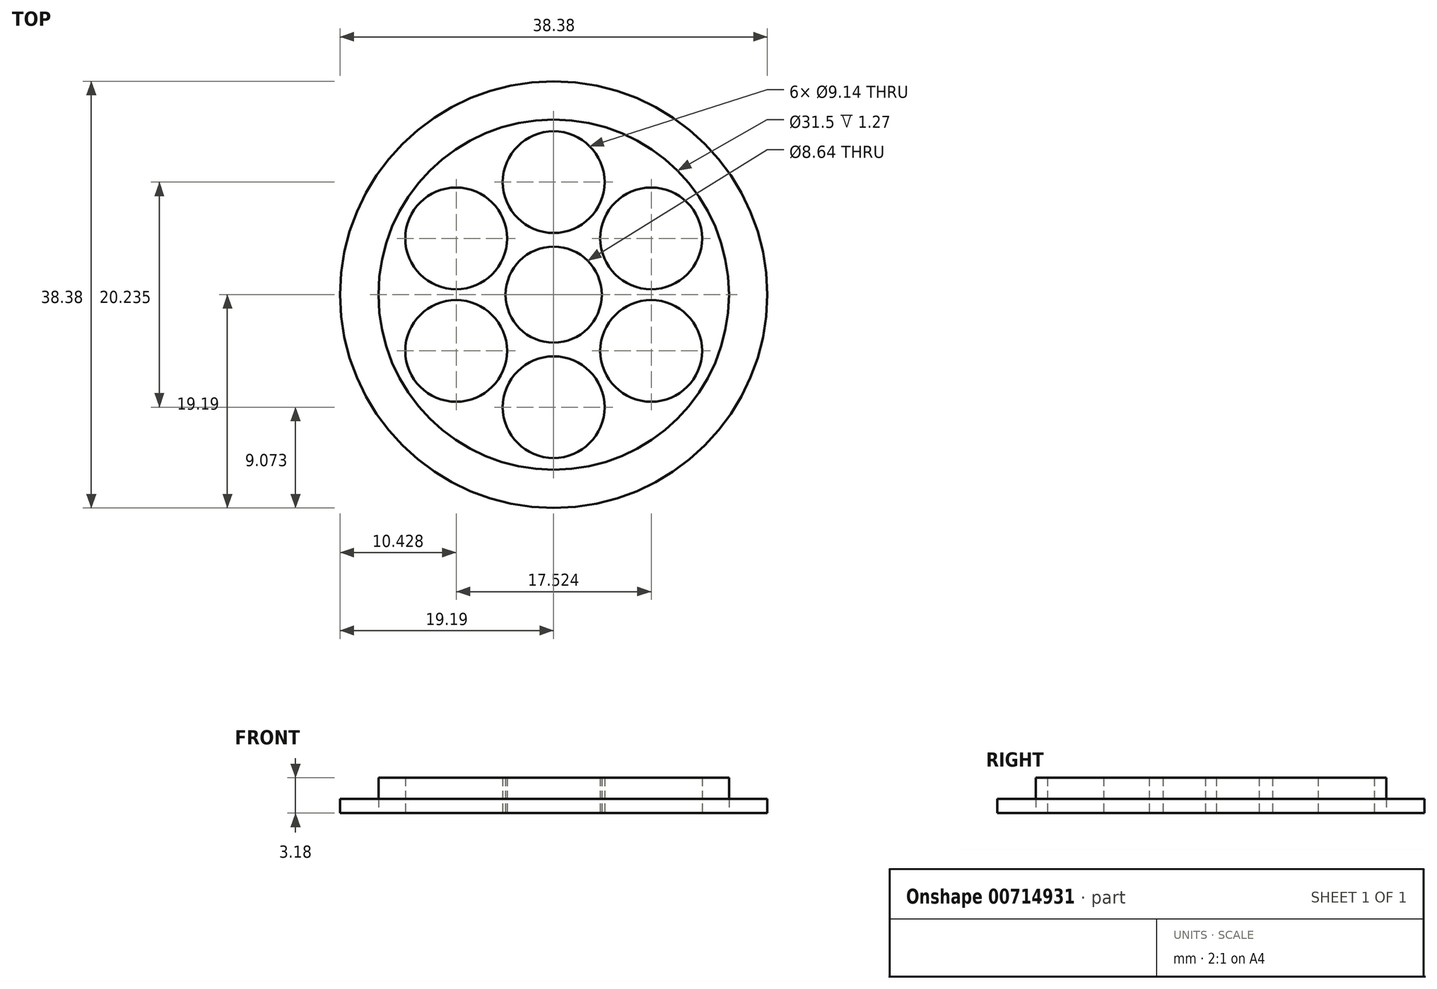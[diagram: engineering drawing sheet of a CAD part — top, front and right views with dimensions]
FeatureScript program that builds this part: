
annotation { "Feature Type Name" : "Feature", "Feature Type Description" : "" }
export const myFeature = defineFeature(function(context is Context, id is Id, definition is map)
    precondition{}
    {
        {
            var Q0;
            Q0=qCreatedBy(makeId("Top.planeOp"),FACE);
            var sketch = newSketch(context, id + "F0", { "sketchPlane" : qUnion([Q0])});
            skCircle(sketch, "E0", {"center": v(0, 0) * mm, "radius": 15.75 * mm});
            skCircle(sketch, "E1", {"center": v(0, 0) * mm, "radius": 19.19 * mm});
            skPoint(sketch, "E2.center", {"position": v(0.47, -0.44) * mm});
            skPoint(sketch, "E3", {"position": v(0, 10.12) * mm});
            skPoint(sketch, "E4.1.0", {"position": v(-8.76, 5.06) * mm});
            skPoint(sketch, "E4.2.0", {"position": v(-8.76, -5.06) * mm});
            skPoint(sketch, "E4.3.0", {"position": v(0, -10.12) * mm});
            skPoint(sketch, "E4.4.0", {"position": v(8.76, -5.06) * mm});
            skPoint(sketch, "E4.5.0", {"position": v(8.76, 5.06) * mm});
            skSolve(sketch);
        }
        {
            var Q0;
            Q0=makeQuery(id+"F0.imprint","IMPRINT",FACE,{"disambiguationData":[TD([[makeQuery(id+"F0.imprint","IMPRINT",EDGE,{"derivedFrom":sQuery(id+"F0.wireOp",EDGE,"E0")}),1.0]])]});
            extrude(context, id + "F1", {"entities" : qUnion([Q0]), "depth" : 3.17 * mm, "offsetDistance" : 25.4 * mm});
        }
        {
            var Q0;
            Q0 = qSketchRegion(id + "F0", true);
            extrude(context, id + "F2", {"entities" : qUnion([Q0]), "depth" : 1.27 * mm, "offsetDistance" : 25.4 * mm});
        }
        {
            var Q0;
            Q0=sQuery(id+"F0.wireOp",VERTEX,"E0.center");
            var Q1;
            Q1=makeQuery(id+"F1.opExtrude","SWEPT_BODY",BODY,{"disambiguationData":[OSD([sQuery(id+"F0.wireOp",EDGE,"E0")])]});
            hole(context, id + "F3", {"style" : HoleStyle.SIMPLE, "endStyle" : HoleEndStyle.THROUGH, "oppositeDirection" : true, "holeDiameter" : 8.64 * mm, "majorDiameter" : 6.35 * mm, "isTappedThrough" : true, "tappedDepth" : 12.7 * mm, "tapClearance" : 3, "locations" : qUnion([Q0]), "scope" : qUnion([Q1])});
        }
        {
            var Q0;
            Q0=sQuery(id+"F0.wireOp",VERTEX,"E3");
            var Q1;
            Q1=sQuery(id+"F0.wireOp",VERTEX,"E4.5.0");
            var Q2;
            Q2=sQuery(id+"F0.wireOp",VERTEX,"E4.4.0");
            var Q3;
            Q3=sQuery(id+"F0.wireOp",VERTEX,"E4.3.0");
            var Q4;
            Q4=sQuery(id+"F0.wireOp",VERTEX,"E4.2.0");
            var Q5;
            Q5=sQuery(id+"F0.wireOp",VERTEX,"E4.1.0");
            var Q6;
            Q6=makeQuery(id+"F1.opExtrude","SWEPT_BODY",BODY,{"disambiguationData":[OSD([sQuery(id+"F0.wireOp",EDGE,"E0")])]});
            hole(context, id + "F4", {"style" : HoleStyle.SIMPLE, "endStyle" : HoleEndStyle.THROUGH, "oppositeDirection" : true, "holeDiameter" : 9.14 * mm, "majorDiameter" : 6.35 * mm, "isTappedThrough" : true, "tappedDepth" : 12.7 * mm, "tapClearance" : 3, "locations" : qUnion([Q0, Q1, Q2, Q3, Q4, Q5]), "scope" : qUnion([Q6])});
        }
    });
